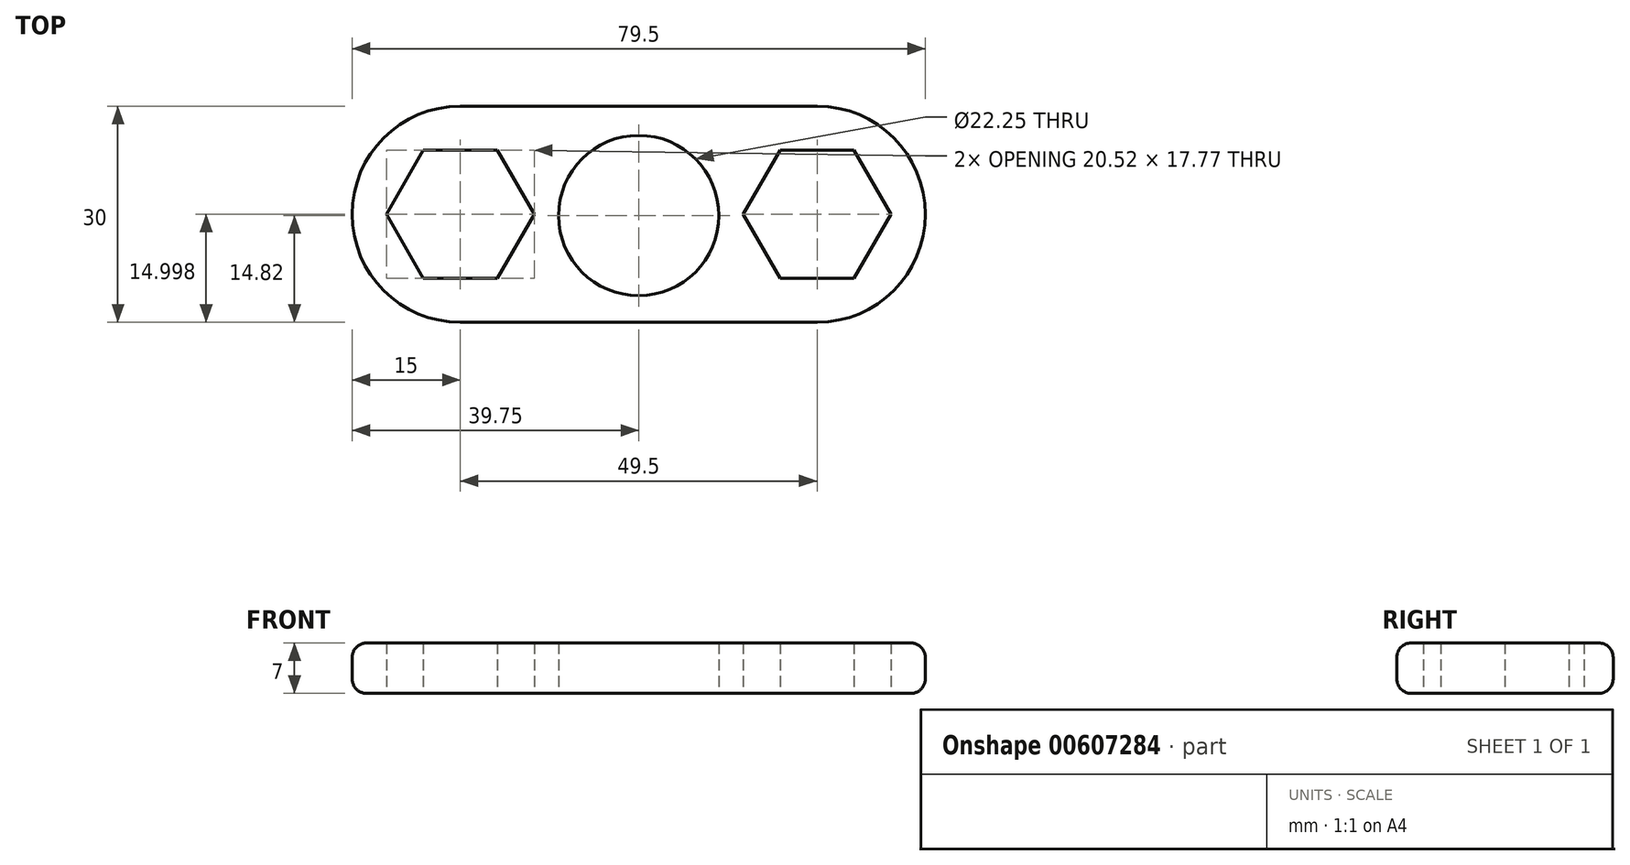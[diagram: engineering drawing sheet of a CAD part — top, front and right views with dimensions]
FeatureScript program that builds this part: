
annotation { "Feature Type Name" : "Feature", "Feature Type Description" : "" }
export const myFeature = defineFeature(function(context is Context, id is Id, definition is map)
    precondition{}
    {
        {
            var Q0;
            Q0=qCreatedBy(makeId("Top.planeOp"),FACE);
            var sketch = newSketch(context, id + "F0", { "sketchPlane" : qUnion([Q0])});
            skCircle(sketch, "E0", {"center": v(0, 0) * mm, "radius": 11.12 * mm});
            skLineSegment(sketch, "E1.bottom", {"start": v(0, 15.18) * mm, "end": v(24.75, 15.18) * mm});
            skLineSegment(sketch, "E1.top", {"start": v(0, -14.82) * mm, "end": v(24.75, -14.82) * mm});
            skLineSegment(sketch, "E1.left", {"start": v(0, 15.18) * mm, "end": v(0, -14.82) * mm});
            skLineSegment(sketch, "E1.right", {"start": v(24.75, 15.18) * mm, "end": v(24.75, -14.82) * mm});
            skLineSegment(sketch, "E2.MirrorCS", {"start": v(0, 15.18) * mm, "end": v(-24.75, 15.18) * mm});
            skLineSegment(sketch, "E3.MirrorCS", {"start": v(-24.75, 15.18) * mm, "end": v(-24.75, -14.82) * mm});
            skLineSegment(sketch, "E4.MirrorCS", {"start": v(0, -14.82) * mm, "end": v(-24.75, -14.82) * mm});
            skCircle(sketch, "E5", {"center": v(24.75, 0.18) * mm, "radius": 15 * mm});
            skCircle(sketch, "E6.MirrorC", {"center": v(-24.75, 0.18) * mm, "radius": 15 * mm});
            skCircle(sketch, "E7.cCircle", {"center": v(-24.75, 0.18) * mm, "radius": 8.88 * mm, "construction": true});
            skLineSegment(sketch, "E7.0", {"start": v(-19.62, -8.7) * mm, "end": v(-29.88, -8.7) * mm});
            skLineSegment(sketch, "E7.1", {"start": v(-29.88, -8.7) * mm, "end": v(-35, 0.18) * mm});
            skLineSegment(sketch, "E7.2", {"start": v(-35, 0.18) * mm, "end": v(-29.88, 9.06) * mm});
            skLineSegment(sketch, "E7.3", {"start": v(-29.88, 9.06) * mm, "end": v(-19.62, 9.06) * mm});
            skLineSegment(sketch, "E7.4", {"start": v(-19.62, 9.06) * mm, "end": v(-14.5, 0.18) * mm});
            skLineSegment(sketch, "E7.5", {"start": v(-14.5, 0.18) * mm, "end": v(-19.62, -8.7) * mm});
            skPoint(sketch, "E7.0.midPoint", {"position": v(-24.75, -8.7) * mm});
            skCircle(sketch, "E8.MirrorC", {"center": v(24.75, 0.18) * mm, "radius": 8.88 * mm, "construction": true});
            skLineSegment(sketch, "E9.MirrorCS", {"start": v(29.88, 9.06) * mm, "end": v(19.62, 9.06) * mm});
            skLineSegment(sketch, "E10.MirrorCS", {"start": v(19.62, 9.06) * mm, "end": v(14.5, 0.18) * mm});
            skLineSegment(sketch, "E11.MirrorCS", {"start": v(14.5, 0.18) * mm, "end": v(19.62, -8.7) * mm});
            skLineSegment(sketch, "E12.MirrorCS", {"start": v(19.62, -8.7) * mm, "end": v(29.88, -8.7) * mm});
            skLineSegment(sketch, "E13.MirrorCS", {"start": v(29.88, -8.7) * mm, "end": v(35, 0.18) * mm});
            skLineSegment(sketch, "E14.MirrorCS", {"start": v(35, 0.18) * mm, "end": v(29.88, 9.06) * mm});
            skSolve(sketch);
        }
        {
            var Q0;
            {var subQ12=sQuery(id+"F0.wireOp",EDGE,"E7.4");Q0=makeQuery(id+"F0.imprint","IMPRINT",FACE,{"disambiguationData":[TD([[makeQuery(id+"F0.imprint","IMPRINT",EDGE,{"derivedFrom":subQ12}),1.0]])]});}
            var Q1;
            {var subQ0=sQuery(id+"F0.wireOp",EDGE,"E7.1");Q1=makeQuery(id+"F0.imprint","IMPRINT",FACE,{"disambiguationData":[TD([[makeQuery(id+"F0.imprint","IMPRINT",EDGE,{"derivedFrom":subQ0}),1.0]])]});}
            var Q2;
            {var subQ5=sQuery(id+"F0.wireOp",EDGE,"E2.MirrorCS");Q2=makeQuery(id+"F0.imprint","IMPRINT",FACE,{"disambiguationData":[TD([[makeQuery(id+"F0.imprint","IMPRINT",EDGE,{"derivedFrom":subQ5}),1.0]])]});}
            var Q3;
            {var subQ5=sQuery(id+"F0.wireOp",EDGE,"E1.bottom");Q3=makeQuery(id+"F0.imprint","IMPRINT",FACE,{"disambiguationData":[TD([[makeQuery(id+"F0.imprint","IMPRINT",EDGE,{"derivedFrom":subQ5}),-1.0]])]});}
            var Q4;
            {var subQ5=sQuery(id+"F0.wireOp",EDGE,"E4.MirrorCS");Q4=makeQuery(id+"F0.imprint","IMPRINT",FACE,{"disambiguationData":[TD([[makeQuery(id+"F0.imprint","IMPRINT",EDGE,{"derivedFrom":subQ5}),-1.0]])]});}
            var Q5;
            {var subQ5=sQuery(id+"F0.wireOp",EDGE,"E1.top");Q5=makeQuery(id+"F0.imprint","IMPRINT",FACE,{"disambiguationData":[TD([[makeQuery(id+"F0.imprint","IMPRINT",EDGE,{"derivedFrom":subQ5}),1.0]])]});}
            var Q6;
            {var subQ12=sQuery(id+"F0.wireOp",EDGE,"E10.MirrorCS");Q6=makeQuery(id+"F0.imprint","IMPRINT",FACE,{"disambiguationData":[TD([[makeQuery(id+"F0.imprint","IMPRINT",EDGE,{"derivedFrom":subQ12}),-1.0]])]});}
            var Q7;
            {var subQ9=sQuery(id+"F0.wireOp",EDGE,"E13.MirrorCS");Q7=makeQuery(id+"F0.imprint","IMPRINT",FACE,{"disambiguationData":[TD([[makeQuery(id+"F0.imprint","IMPRINT",EDGE,{"derivedFrom":subQ9}),-1.0]])]});}
            extrude(context, id + "F1", {"entities" : qUnion([Q0, Q1, Q2, Q3, Q4, Q5, Q6, Q7]), "depth" : 7 * mm, "offsetDistance" : 25 * mm});
        }
        {
            var Q0;
            Q0=makeQuery(id+"F1.opExtrude","CAP_EDGE",EDGE,{"disambiguationData":[OSD([sQuery(id+"F0.wireOp",EDGE,"E1.bottom"),sQuery(id+"F0.wireOp",EDGE,"E2.MirrorCS")])],"isStart":false});
            var Q1;
            Q1=makeQuery(id+"F1.opExtrude","CAP_EDGE",EDGE,{"disambiguationData":[OSD([sQuery(id+"F0.wireOp",EDGE,"E1.bottom"),sQuery(id+"F0.wireOp",EDGE,"E2.MirrorCS")])],"isStart":true});
            fillet(context, id + "F2", {"entities" : qUnion([Q0, Q1]), "radius" : 2 * mm, "tangentPropagation" : true, "allowEdgeOverflow" : false});
        }
    });
